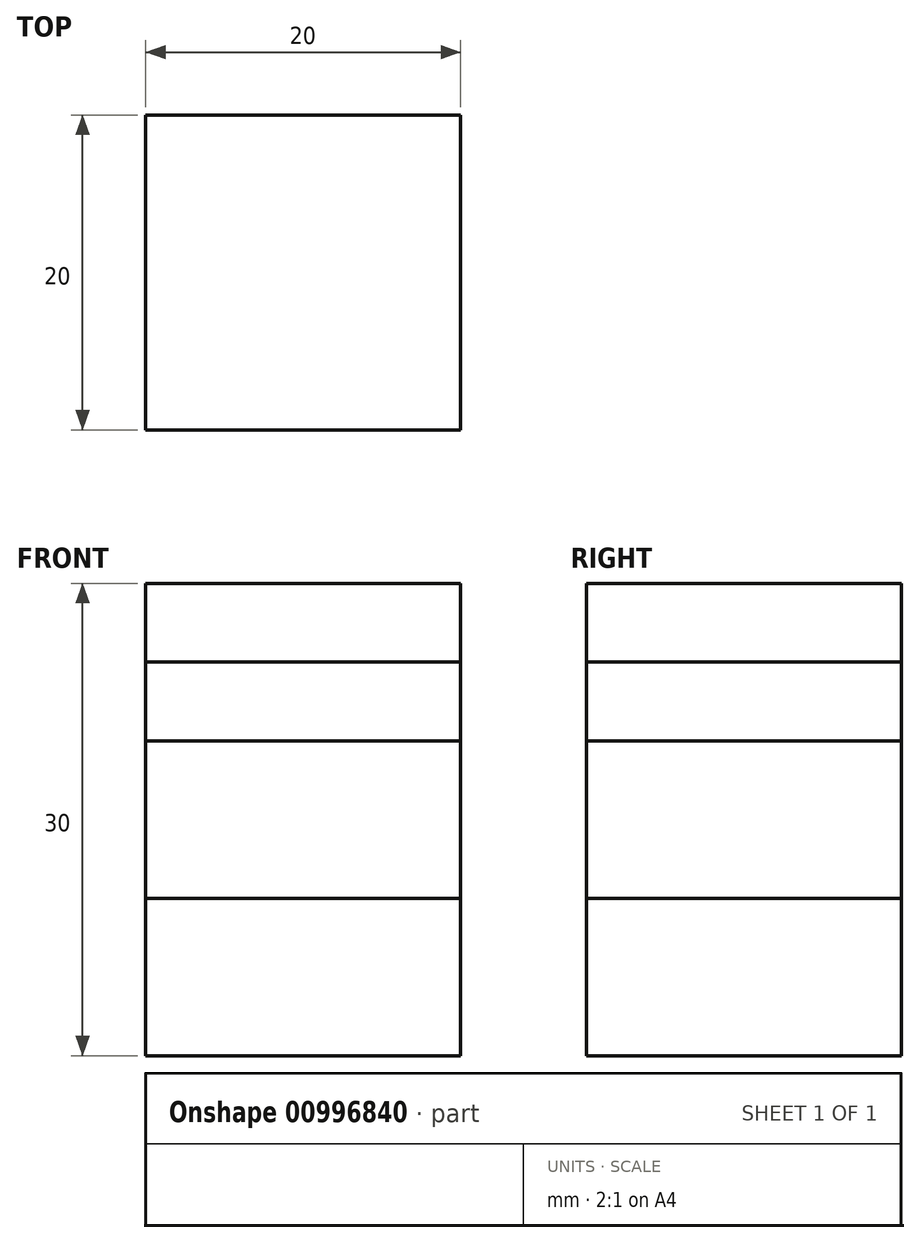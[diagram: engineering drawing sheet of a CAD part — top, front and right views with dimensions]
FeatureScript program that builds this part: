
annotation { "Feature Type Name" : "Feature", "Feature Type Description" : "" }
export const myFeature = defineFeature(function(context is Context, id is Id, definition is map)
    precondition{}
    {
        {
            var Q0;
            Q0=qCreatedBy(makeId("Top.planeOp"),FACE);
            var sketch = newSketch(context, id + "F0", { "sketchPlane" : qUnion([Q0])});
            skLineSegment(sketch, "E0.bottom", {"start": v(10, -10) * mm, "end": v(-10, -10) * mm});
            skLineSegment(sketch, "E0.top", {"start": v(10, 10) * mm, "end": v(-10, 10) * mm});
            skLineSegment(sketch, "E0.left", {"start": v(10, -10) * mm, "end": v(10, 10) * mm});
            skLineSegment(sketch, "E0.right", {"start": v(-10, -10) * mm, "end": v(-10, 10) * mm});
            skPoint(sketch, "E0.middle", {"position": v(0, 0) * mm});
            skSolve(sketch);
        }
        {
            var Q0;
            Q0 = qSketchRegion(id + "F0", true);
            extrude(context, id + "F1", {"entities" : qUnion([Q0]), "depth" : 10 * mm, "offsetDistance" : 25 * mm});
        }
        {
            var Q0;
            Q0=makeQuery(id+"F1.opExtrude","CAP_FACE",FACE,{"disambiguationData":[OSD([sQuery(id+"F0.wireOp",EDGE,"E0.bottom"),sQuery(id+"F0.wireOp",EDGE,"E0.top"),sQuery(id+"F0.wireOp",EDGE,"E0.left"),sQuery(id+"F0.wireOp",EDGE,"E0.right")])],"isStart":false});
            extrude(context, id + "F2", {"entities" : qUnion([Q0]), "depth" : 10 * mm, "offsetDistance" : 25 * mm});
        }
        {
            var Q0;
            Q0=makeQuery(id+"F2.opExtrude","CAP_FACE",FACE,{"disambiguationData":[OSD([sQuery(id+"F0.wireOp",EDGE,"E0.bottom"),sQuery(id+"F0.wireOp",EDGE,"E0.top"),sQuery(id+"F0.wireOp",EDGE,"E0.left"),sQuery(id+"F0.wireOp",EDGE,"E0.right")])],"isStart":false});
            extrude(context, id + "F3", {"entities" : qUnion([Q0]), "depth" : 5 * mm, "offsetDistance" : 25 * mm});
        }
        {
            var Q0;
            Q0=makeQuery(id+"F3.opExtrude","CAP_FACE",FACE,{"disambiguationData":[OSD([sQuery(id+"F0.wireOp",EDGE,"E0.bottom"),sQuery(id+"F0.wireOp",EDGE,"E0.top"),sQuery(id+"F0.wireOp",EDGE,"E0.left"),sQuery(id+"F0.wireOp",EDGE,"E0.right")])],"isStart":false});
            extrude(context, id + "F4", {"entities" : qUnion([Q0]), "depth" : 5 * mm, "offsetDistance" : 25 * mm});
        }
    });
